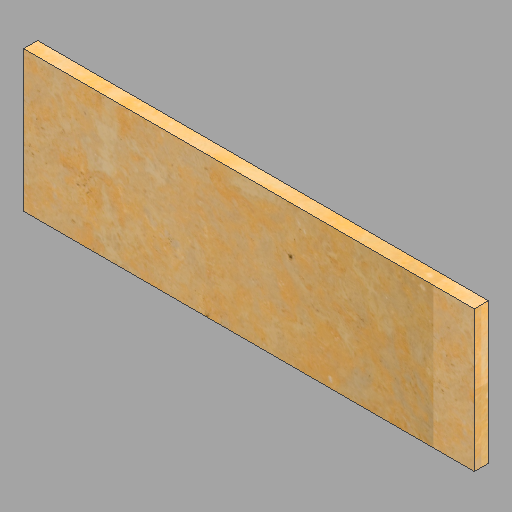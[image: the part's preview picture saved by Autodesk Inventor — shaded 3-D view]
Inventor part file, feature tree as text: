
AUTODESK INVENTOR PART (.ipt)
format: ipt  version: 2023 (Build 270158030, 158C)  size: 448,000 bytes
history: native  units: in
note: dims shown in document units (in); Inventor stores cm internally (conversion verified against a paired STEP export)
features: extrude x1, sketch x1
ambient origin geometry x8: Origin, YZ Plane, XZ Plane, XY Plane, X Axis, Y Axis, Z Axis, Center Point
bodies: Solid1 (feature_tree)
feature tree (2):
  extrude  "Extrusion1"  Depth=1.0in
  sketch  "Sketch1"  dims[d0=10.0in d1=1.0in d2=32.0in d3=0.0in]
